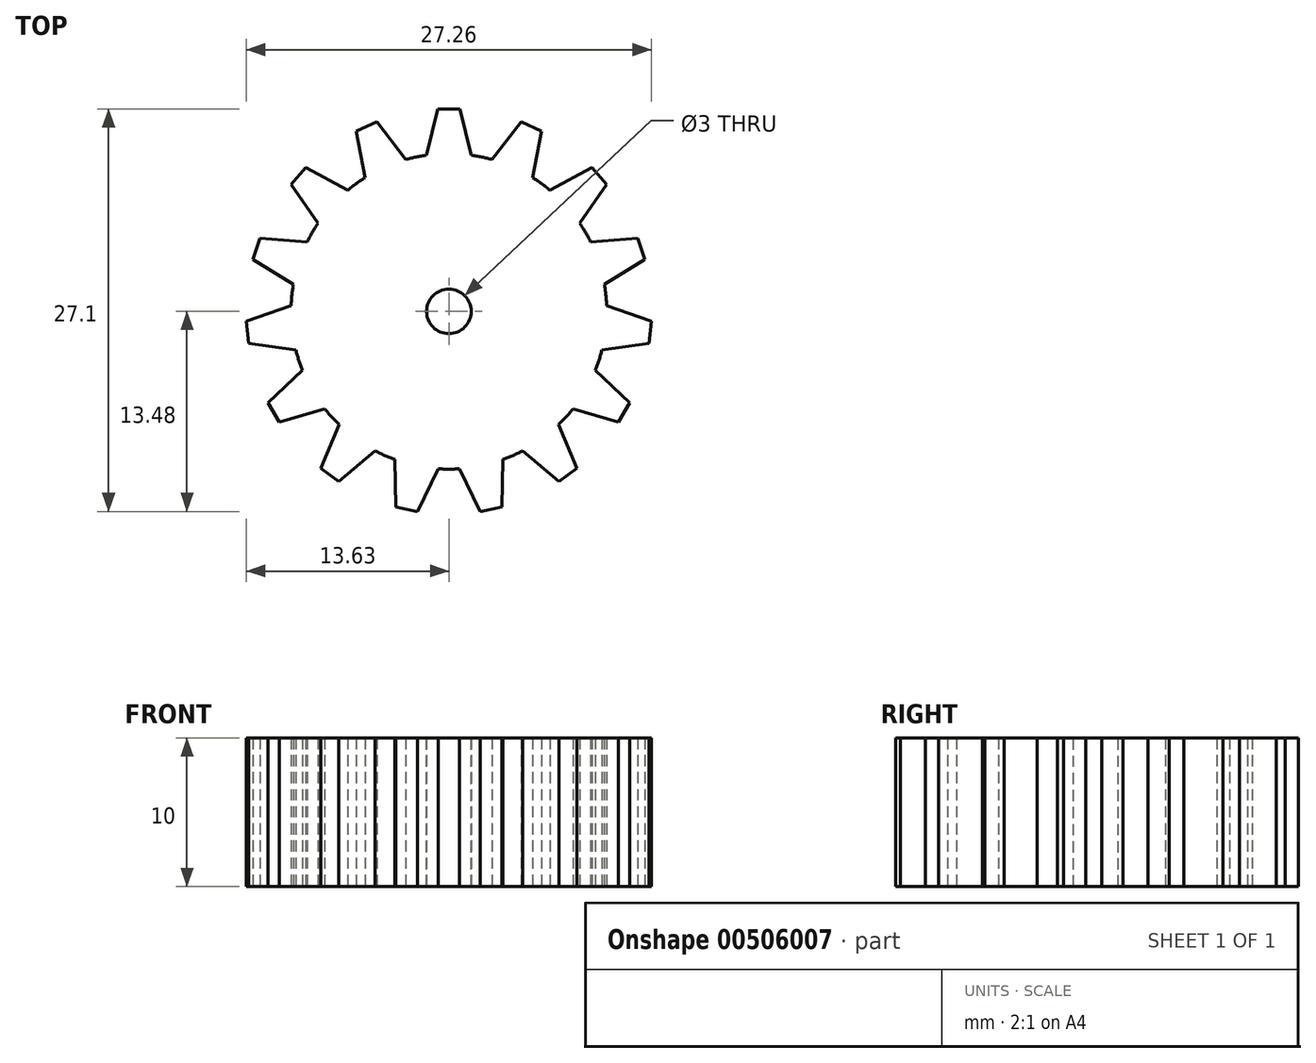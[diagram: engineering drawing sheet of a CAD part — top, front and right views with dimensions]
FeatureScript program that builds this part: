
annotation { "Feature Type Name" : "Feature", "Feature Type Description" : "" }
export const myFeature = defineFeature(function(context is Context, id is Id, definition is map)
    precondition{}
    {
        {
            var Q0;
            Q0=qCreatedBy(makeId("Top.planeOp"),FACE);
            var sketch = newSketch(context, id + "F0", { "sketchPlane" : qUnion([Q0])});
            skCircle(sketch, "E0", {"center": v(0, 0) * mm, "radius": 10.62 * mm});
            skLineSegment(sketch, "E1", {"start": v(0, 13.63) * mm, "end": v(0.75, 13.63) * mm});
            skLineSegment(sketch, "E2", {"start": v(0.75, 13.63) * mm, "end": v(1.5, 10.52) * mm});
            skLineSegment(sketch, "E3.MirrorCS", {"start": v(0, 13.63) * mm, "end": v(-0.75, 13.63) * mm});
            skLineSegment(sketch, "E4.MirrorCS", {"start": v(-0.75, 13.63) * mm, "end": v(-1.5, 10.52) * mm});
            skLineSegment(sketch, "E5.1.0", {"start": v(-5.54, 12.45) * mm, "end": v(-4.86, 12.75) * mm});
            skLineSegment(sketch, "E5.1.1", {"start": v(-4.86, 12.75) * mm, "end": v(-2.91, 10.22) * mm});
            skLineSegment(sketch, "E5.1.2", {"start": v(-5.54, 12.45) * mm, "end": v(-6.23, 12.14) * mm});
            skLineSegment(sketch, "E5.1.3", {"start": v(-6.23, 12.14) * mm, "end": v(-5.64, 9) * mm});
            skLineSegment(sketch, "E5.2.0", {"start": v(-10.13, 9.12) * mm, "end": v(-9.62, 9.67) * mm});
            skLineSegment(sketch, "E5.2.1", {"start": v(-9.62, 9.67) * mm, "end": v(-6.82, 8.15) * mm});
            skLineSegment(sketch, "E5.2.2", {"start": v(-10.13, 9.12) * mm, "end": v(-10.63, 8.56) * mm});
            skLineSegment(sketch, "E5.2.3", {"start": v(-10.63, 8.56) * mm, "end": v(-8.82, 5.93) * mm});
            skLineSegment(sketch, "E5.3.0", {"start": v(-12.96, 4.21) * mm, "end": v(-12.73, 4.92) * mm});
            skLineSegment(sketch, "E5.3.1", {"start": v(-12.73, 4.92) * mm, "end": v(-9.54, 4.67) * mm});
            skLineSegment(sketch, "E5.3.2", {"start": v(-12.96, 4.21) * mm, "end": v(-13.19, 3.5) * mm});
            skLineSegment(sketch, "E5.3.3", {"start": v(-13.19, 3.5) * mm, "end": v(-10.47, 1.83) * mm});
            skLineSegment(sketch, "E5.4.0", {"start": v(-13.55, -1.42) * mm, "end": v(-13.63, -0.68) * mm});
            skLineSegment(sketch, "E5.4.1", {"start": v(-13.63, -0.68) * mm, "end": v(-10.62, 0.39) * mm});
            skLineSegment(sketch, "E5.4.2", {"start": v(-13.55, -1.42) * mm, "end": v(-13.47, -2.17) * mm});
            skLineSegment(sketch, "E5.4.3", {"start": v(-13.47, -2.17) * mm, "end": v(-10.3, -2.59) * mm});
            skLineSegment(sketch, "E5.5.0", {"start": v(-11.8, -6.81) * mm, "end": v(-12.17, -6.16) * mm});
            skLineSegment(sketch, "E5.5.1", {"start": v(-12.17, -6.16) * mm, "end": v(-9.86, -3.96) * mm});
            skLineSegment(sketch, "E5.5.2", {"start": v(-11.8, -6.81) * mm, "end": v(-11.42, -7.46) * mm});
            skLineSegment(sketch, "E5.5.3", {"start": v(-11.42, -7.46) * mm, "end": v(-8.36, -6.55) * mm});
            skLineSegment(sketch, "E5.6.0", {"start": v(-8, -11.02) * mm, "end": v(-8.62, -10.58) * mm});
            skLineSegment(sketch, "E5.6.1", {"start": v(-8.62, -10.58) * mm, "end": v(-7.4, -7.63) * mm});
            skLineSegment(sketch, "E5.6.2", {"start": v(-8, -11.02) * mm, "end": v(-7.4, -11.46) * mm});
            skLineSegment(sketch, "E5.6.3", {"start": v(-7.4, -11.46) * mm, "end": v(-4.97, -9.39) * mm});
            skLineSegment(sketch, "E5.7.0", {"start": v(-2.83, -13.33) * mm, "end": v(-3.57, -13.17) * mm});
            skLineSegment(sketch, "E5.7.1", {"start": v(-3.57, -13.17) * mm, "end": v(-3.65, -9.98) * mm});
            skLineSegment(sketch, "E5.7.2", {"start": v(-2.83, -13.33) * mm, "end": v(-2.1, -13.48) * mm});
            skLineSegment(sketch, "E5.7.3", {"start": v(-2.1, -13.48) * mm, "end": v(-0.72, -10.6) * mm});
            skLineSegment(sketch, "E5.8.0", {"start": v(2.83, -13.33) * mm, "end": v(2.1, -13.48) * mm});
            skLineSegment(sketch, "E5.8.1", {"start": v(2.1, -13.48) * mm, "end": v(0.72, -10.6) * mm});
            skLineSegment(sketch, "E5.8.2", {"start": v(2.83, -13.33) * mm, "end": v(3.57, -13.17) * mm});
            skLineSegment(sketch, "E5.8.3", {"start": v(3.57, -13.17) * mm, "end": v(3.65, -9.98) * mm});
            skLineSegment(sketch, "E5.9.0", {"start": v(8, -11.02) * mm, "end": v(7.4, -11.46) * mm});
            skLineSegment(sketch, "E5.9.1", {"start": v(7.4, -11.46) * mm, "end": v(4.97, -9.39) * mm});
            skLineSegment(sketch, "E5.9.2", {"start": v(8, -11.02) * mm, "end": v(8.62, -10.58) * mm});
            skLineSegment(sketch, "E5.9.3", {"start": v(8.62, -10.58) * mm, "end": v(7.4, -7.63) * mm});
            skLineSegment(sketch, "E5.10.0", {"start": v(11.8, -6.81) * mm, "end": v(11.42, -7.46) * mm});
            skLineSegment(sketch, "E5.10.1", {"start": v(11.42, -7.46) * mm, "end": v(8.36, -6.55) * mm});
            skLineSegment(sketch, "E5.10.2", {"start": v(11.8, -6.81) * mm, "end": v(12.17, -6.16) * mm});
            skLineSegment(sketch, "E5.10.3", {"start": v(12.17, -6.16) * mm, "end": v(9.86, -3.96) * mm});
            skLineSegment(sketch, "E5.11.0", {"start": v(13.55, -1.42) * mm, "end": v(13.47, -2.17) * mm});
            skLineSegment(sketch, "E5.11.1", {"start": v(13.47, -2.17) * mm, "end": v(10.3, -2.59) * mm});
            skLineSegment(sketch, "E5.11.2", {"start": v(13.55, -1.42) * mm, "end": v(13.63, -0.68) * mm});
            skLineSegment(sketch, "E5.11.3", {"start": v(13.63, -0.68) * mm, "end": v(10.62, 0.39) * mm});
            skLineSegment(sketch, "E5.12.0", {"start": v(12.96, 4.21) * mm, "end": v(13.19, 3.5) * mm});
            skLineSegment(sketch, "E5.12.1", {"start": v(13.19, 3.5) * mm, "end": v(10.47, 1.83) * mm});
            skLineSegment(sketch, "E5.12.2", {"start": v(12.96, 4.21) * mm, "end": v(12.73, 4.92) * mm});
            skLineSegment(sketch, "E5.12.3", {"start": v(12.73, 4.92) * mm, "end": v(9.54, 4.67) * mm});
            skLineSegment(sketch, "E5.13.0", {"start": v(10.13, 9.12) * mm, "end": v(10.63, 8.56) * mm});
            skLineSegment(sketch, "E5.13.1", {"start": v(10.63, 8.56) * mm, "end": v(8.82, 5.93) * mm});
            skLineSegment(sketch, "E5.13.2", {"start": v(10.13, 9.12) * mm, "end": v(9.62, 9.67) * mm});
            skLineSegment(sketch, "E5.13.3", {"start": v(9.62, 9.67) * mm, "end": v(6.82, 8.15) * mm});
            skLineSegment(sketch, "E5.14.0", {"start": v(5.54, 12.45) * mm, "end": v(6.23, 12.14) * mm});
            skLineSegment(sketch, "E5.14.1", {"start": v(6.23, 12.14) * mm, "end": v(5.64, 9) * mm});
            skLineSegment(sketch, "E5.14.2", {"start": v(5.54, 12.45) * mm, "end": v(4.86, 12.75) * mm});
            skLineSegment(sketch, "E5.14.3", {"start": v(4.86, 12.75) * mm, "end": v(2.91, 10.22) * mm});
            skSolve(sketch);
        }
        {
            var Q0;
            Q0 = qSketchRegion(id + "F0", true);
            extrude(context, id + "F1", {"entities" : qUnion([Q0]), "depth" : 10 * mm, "offsetDistance" : 25 * mm});
        }
        {
            var Q0;
            Q0=makeQuery(id+"F1.opExtrude","CAP_FACE",FACE,{"disambiguationData":[OSD([sQuery(id+"F0.wireOp",EDGE,"E0"),sQuery(id+"F0.wireOp",EDGE,"E1"),sQuery(id+"F0.wireOp",EDGE,"E2"),sQuery(id+"F0.wireOp",EDGE,"E3.MirrorCS"),sQuery(id+"F0.wireOp",EDGE,"E4.MirrorCS"),sQuery(id+"F0.wireOp",EDGE,"E5.1.0"),sQuery(id+"F0.wireOp",EDGE,"E5.1.1"),sQuery(id+"F0.wireOp",EDGE,"E5.1.2"),sQuery(id+"F0.wireOp",EDGE,"E5.1.3"),sQuery(id+"F0.wireOp",EDGE,"E5.2.0"),sQuery(id+"F0.wireOp",EDGE,"E5.2.1"),sQuery(id+"F0.wireOp",EDGE,"E5.2.2"),sQuery(id+"F0.wireOp",EDGE,"E5.2.3"),sQuery(id+"F0.wireOp",EDGE,"E5.3.0"),sQuery(id+"F0.wireOp",EDGE,"E5.3.1"),sQuery(id+"F0.wireOp",EDGE,"E5.3.2"),sQuery(id+"F0.wireOp",EDGE,"E5.3.3"),sQuery(id+"F0.wireOp",EDGE,"E5.4.0"),sQuery(id+"F0.wireOp",EDGE,"E5.4.1"),sQuery(id+"F0.wireOp",EDGE,"E5.4.2"),sQuery(id+"F0.wireOp",EDGE,"E5.4.3"),sQuery(id+"F0.wireOp",EDGE,"E5.5.0"),sQuery(id+"F0.wireOp",EDGE,"E5.5.1"),sQuery(id+"F0.wireOp",EDGE,"E5.5.2"),sQuery(id+"F0.wireOp",EDGE,"E5.5.3"),sQuery(id+"F0.wireOp",EDGE,"E5.6.0"),sQuery(id+"F0.wireOp",EDGE,"E5.6.1"),sQuery(id+"F0.wireOp",EDGE,"E5.6.2"),sQuery(id+"F0.wireOp",EDGE,"E5.6.3"),sQuery(id+"F0.wireOp",EDGE,"E5.7.0"),sQuery(id+"F0.wireOp",EDGE,"E5.7.1"),sQuery(id+"F0.wireOp",EDGE,"E5.7.2"),sQuery(id+"F0.wireOp",EDGE,"E5.7.3"),sQuery(id+"F0.wireOp",EDGE,"E5.8.0"),sQuery(id+"F0.wireOp",EDGE,"E5.8.1"),sQuery(id+"F0.wireOp",EDGE,"E5.8.2"),sQuery(id+"F0.wireOp",EDGE,"E5.8.3"),sQuery(id+"F0.wireOp",EDGE,"E5.9.0"),sQuery(id+"F0.wireOp",EDGE,"E5.9.1"),sQuery(id+"F0.wireOp",EDGE,"E5.9.2"),sQuery(id+"F0.wireOp",EDGE,"E5.9.3"),sQuery(id+"F0.wireOp",EDGE,"E5.10.0"),sQuery(id+"F0.wireOp",EDGE,"E5.10.1"),sQuery(id+"F0.wireOp",EDGE,"E5.10.2"),sQuery(id+"F0.wireOp",EDGE,"E5.10.3"),sQuery(id+"F0.wireOp",EDGE,"E5.11.0"),sQuery(id+"F0.wireOp",EDGE,"E5.11.1"),sQuery(id+"F0.wireOp",EDGE,"E5.11.2"),sQuery(id+"F0.wireOp",EDGE,"E5.11.3"),sQuery(id+"F0.wireOp",EDGE,"E5.12.0"),sQuery(id+"F0.wireOp",EDGE,"E5.12.1"),sQuery(id+"F0.wireOp",EDGE,"E5.12.2"),sQuery(id+"F0.wireOp",EDGE,"E5.12.3"),sQuery(id+"F0.wireOp",EDGE,"E5.13.0"),sQuery(id+"F0.wireOp",EDGE,"E5.13.1"),sQuery(id+"F0.wireOp",EDGE,"E5.13.2"),sQuery(id+"F0.wireOp",EDGE,"E5.13.3"),sQuery(id+"F0.wireOp",EDGE,"E5.14.0"),sQuery(id+"F0.wireOp",EDGE,"E5.14.1"),sQuery(id+"F0.wireOp",EDGE,"E5.14.2"),sQuery(id+"F0.wireOp",EDGE,"E5.14.3")])],"isStart":false});
            var sketch = newSketch(context, id + "F2", { "sketchPlane" : qUnion([Q0])});
            skCircle(sketch, "E6", {"center": v(0, 0) * mm, "radius": 1.5 * mm});
            skSolve(sketch);
        }
        {
            var Q0;
            Q0 = qSketchRegion(id + "F2", true);
            extrude(context, id + "F3", {"entities" : qUnion([Q0]), "operationType" : NewBodyOperationType.REMOVE, "endBound" : BoundingType.THROUGH_ALL, "oppositeDirection" : true, "depth" : 25 * mm, "offsetDistance" : 25 * mm});
        }
    });
